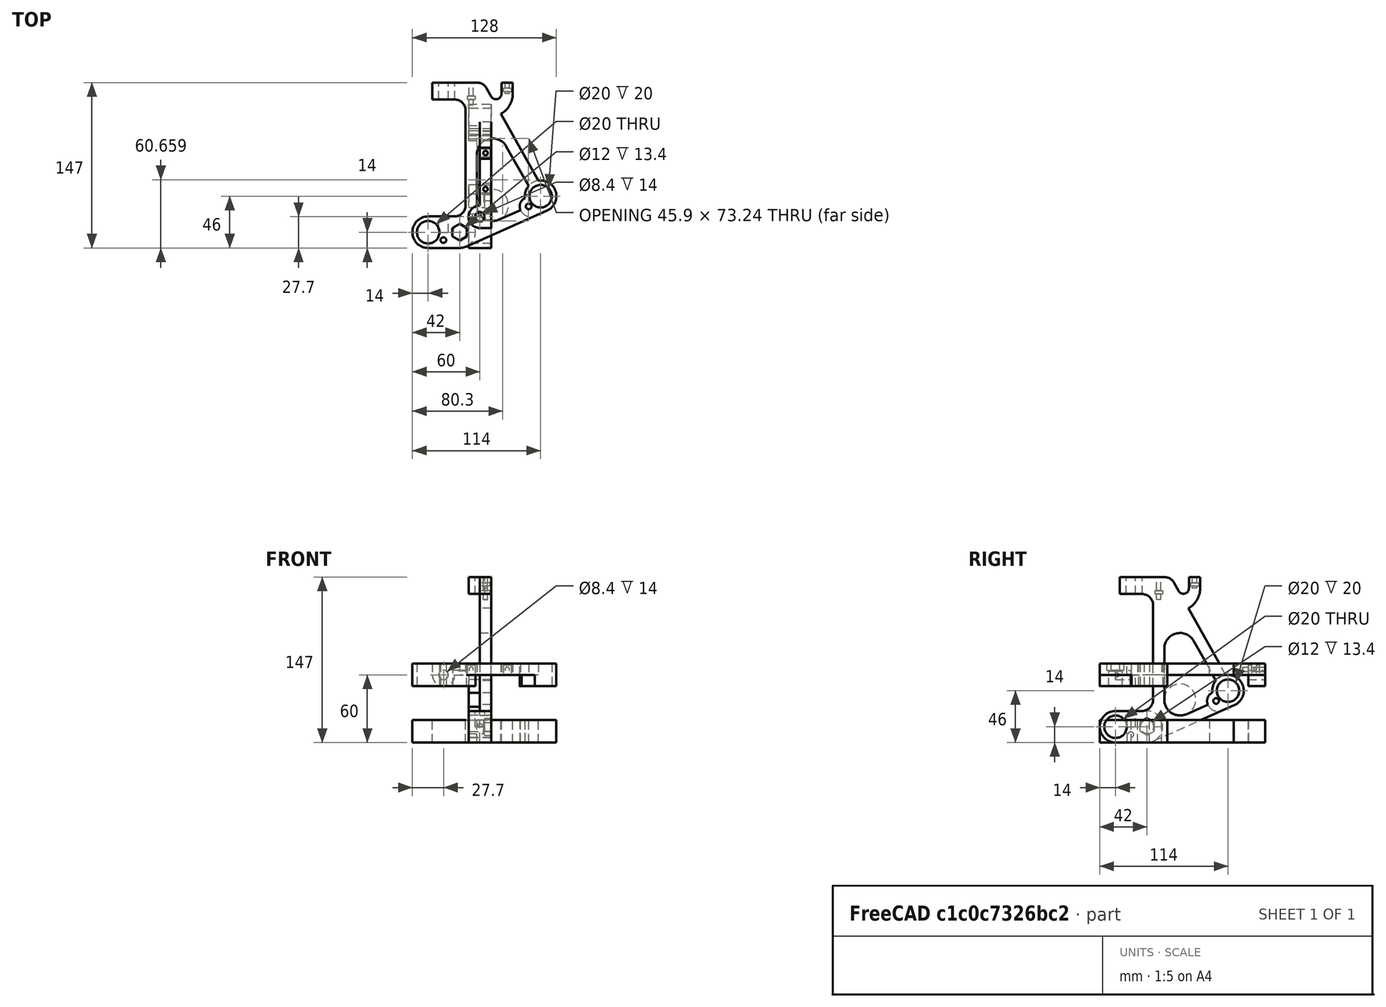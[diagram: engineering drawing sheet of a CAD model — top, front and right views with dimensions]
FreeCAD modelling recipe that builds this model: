
FCSTD DOCUMENT  (FreeCAD 0.15R4527 (Git))
Label: x_carriage_right
License: All rights reserved
LicenseURL: http://en.wikipedia.org/wiki/All_rights_reserved
objects: Part::Cylinder×10, Part::MultiFuse×8, Part::Cut×5, Part::Feature×3, Sketcher::SketchObject×2, Part::Box×2, Part::Extrusion×1, PartDesign::Pocket×1, Mesh::Feature×1, Part::Mirroring×1, Part::Prism×1
note: 35 computed .brp shape members not serialized (recipe doc carries the construction recipe); baked Part::Feature solids carry a one-line shape summary decoded from their .brp

FEATURE [Part::Feature] Xcariageleft001001  label="Xcariageleft002"
  shape: bbox 128 x 147 x 20 mm, 1927 faces, 0 solids (baked)
FEATURE [Sketcher::SketchObject] Sketch
  ExternalGeometry = -> [Xcariageleft001001]
  Placement = pos=(0,0,3.8147e-06) rot=(1,0,0;3.14159rad)
  Support = -> Xcariageleft001001 [Face866]
  sketch-geometry (27):
    g0: LineSegment StartX=14 StartY=-3e-12 StartZ=0 EndX=42 EndY=1e-12 EndZ=0
    g1: LineSegment StartX=47.6883 StartY=-1.20767 StartZ=0 EndX=119.688 EndY=-33.2233 EndZ=0
    g2: LineSegment StartX=111.977 StartY=-59.8687 StartZ=0 EndX=78.7678 EndY=-119.207 EndZ=0
    g3: LineSegment StartX=83.5669 StartY=-90.1556 StartZ=0 EndX=103.25 EndY=-54.9849 EndZ=0
    g4: LineSegment StartX=96.0562 StartY=-33.6591 StartZ=0 EndX=77.0383 EndY=-25.2025 EndZ=0
    g5: LineSegment StartX=57.35 StartY=-37.9949 StartZ=0 EndX=57.35 EndY=-83.3184 EndZ=0
    g6: LineSegment StartX=14 StartY=-28 StartZ=0 EndX=37.35 EndY=-28 EndZ=0
    g7: LineSegment StartX=47.35 StartY=-38 StartZ=0 EndX=47.35 EndY=-122 EndZ=0
    g8: LineSegment StartX=37.35 StartY=-132 StartZ=0 EndX=17.7 EndY=-132 EndZ=0
    g9: ArcOfCircle CenterX=114 CenterY=-46.0156 CenterZ=0 NormalX=0 NormalY=0 NormalZ=1 Radius=14 StartAngle=4.56737 EndAngle=7.43558
    g10: ArcOfCircle CenterX=103.366 CenterY=-36.9095 CenterZ=0 NormalX=0 NormalY=0 NormalZ=1 Radius=8.00001 StartAngle=2.72319 EndAngle=4.29398
    g11: ArcOfCircle CenterX=114 CenterY=-46.0156 CenterZ=0 NormalX=0 NormalY=0 NormalZ=1 Radius=14 StartAngle=3.01294 EndAngle=3.83695
    g12: ArcOfCircle CenterX=71.35 CenterY=-83.3184 CenterZ=0 NormalX=0 NormalY=0 NormalZ=1 Radius=14 StartAngle=3.14159 EndAngle=5.77296
    g13: ArcOfCircle CenterX=68.8096 CenterY=-137 CenterZ=0 NormalX=0 NormalY=0 NormalZ=1 Radius=20.3904 StartAngle=2.53065e-07 EndAngle=1.06057
    g14: ArcOfCircle CenterX=74.3581 CenterY=-137 CenterZ=0 NormalX=0 NormalY=0 NormalZ=1 Radius=4.84187 StartAngle=1.80253e-06 EndAngle=2.63136
    g15: ArcOfCircle CenterX=57.35 CenterY=-137 CenterZ=0 NormalX=0 NormalY=0 NormalZ=1 Radius=10 StartAngle=4.71239 EndAngle=5.77295
    g16: ArcOfCircle CenterX=37.35 CenterY=-122 CenterZ=0 NormalX=0 NormalY=0 NormalZ=1 Radius=10 StartAngle=4.71239 EndAngle=6.28318
    g17: ArcOfCircle CenterX=71.35 CenterY=-37.9949 CenterZ=0 NormalX=0 NormalY=0 NormalZ=1 Radius=14 StartAngle=1.15239 EndAngle=3.14159
    g18: ArcOfCircle CenterX=37.35 CenterY=-38 CenterZ=0 NormalX=0 NormalY=0 NormalZ=1 Radius=10 StartAngle=6.16e-10 EndAngle=1.5708
    g19: ArcOfCircle CenterX=42 CenterY=-13.9999 CenterZ=0 NormalX=0 NormalY=0 NormalZ=1 Radius=13.9999 StartAngle=1.15239 EndAngle=1.5708
    g20: ArcOfCircle CenterX=14 CenterY=-14 CenterZ=0 NormalX=0 NormalY=0 NormalZ=1 Radius=14 StartAngle=1.5708 EndAngle=4.71239
    g21: LineSegment StartX=17.7 StartY=-132 StartZ=0 EndX=17.7 EndY=-147 EndZ=0
    g22: LineSegment StartX=17.7 StartY=-147 StartZ=0 EndX=57.35 EndY=-147 EndZ=0
    g23: LineSegment StartX=70.133 StartY=-134.635 StartZ=0 EndX=66.0763 EndY=-141.884 EndZ=0
    g24: LineSegment StartX=79.2 StartY=-137 StartZ=0 EndX=79.2 EndY=-147 EndZ=0
    g25: LineSegment StartX=89.2 StartY=-137 StartZ=0 EndX=89.2 EndY=-147 EndZ=0
    g26: LineSegment StartX=79.2 StartY=-147 StartZ=0 EndX=89.2 EndY=-147 EndZ=0
  constraints (66):
    c: Coincident(g0,g-4)
    c: Coincident(g0,g-4)
    c: Coincident(g1,g-3)
    c: Coincident(g1,g-3)
    c: Coincident(g2,g-9)
    c: Coincident(g2,g-9)
    c: Coincident(g3,g-8)
    c: Coincident(g3,g-8)
    c: Coincident(g4,g-17)
    c: Coincident(g4,g-17)
    c: Coincident(g5,g-7)
    c: Coincident(g5,g-7)
    c: Coincident(g6,g-5)
    c: Coincident(g6,g-5)
    c: Coincident(g7,g-6)
    c: Coincident(g7,g-6)
    c: Coincident(g8,g-16)
    c: Coincident(g8,g-16)
    c: Coincident(g9,g2)
    c: Coincident(g9,g1)
    c: PointOnObject(g-22,g9)
    c: Coincident(g10,g-20)
    c: Coincident(g10,g4)
    c: PointOnObject(g-19,g10)
    c: Coincident(g11,g10)
    c: Coincident(g11,g3)
    c: PointOnObject(g-21,g11)
    c: Coincident(g12,g5)
    c: Coincident(g12,g3)
    c: PointOnObject(g-27,g12)
    c: Coincident(g13,g2)
    c: Coincident(g13,g-10)
    c: PointOnObject(g-23,g13)
    c: Coincident(g14,g-13)
    c: Coincident(g14,g-12)
    c: PointOnObject(g-24,g14)
    c: Coincident(g15,g-13)
    c: Coincident(g15,g-14)
    c: PointOnObject(g-25,g15)
    c: Coincident(g16,g8)
    c: Coincident(g16,g7)
    c: PointOnObject(g-26,g16)
    c: Coincident(g17,g5)
    c: Coincident(g17,g4)
    c: PointOnObject(g-18,g17)
    c: Coincident(g18,g7)
    c: Coincident(g18,g6)
    c: PointOnObject(g-28,g18)
    c: Coincident(g19,g1)
    c: Coincident(g19,g0)
    c: PointOnObject(g-30,g19)
    c: Coincident(g20,g6)
    c: Coincident(g20,g0)
    c: PointOnObject(g-29,g20)
    c: Coincident(g21,g8)
    c: Coincident(g21,g-15)
    c: Coincident(g22,g21)
    c: Coincident(g22,g15)
    c: Coincident(g23,g14)
    c: Coincident(g23,g15)
    c: Coincident(g24,g14)
    c: Coincident(g24,g-12)
    c: Coincident(g25,g13)
    c: Coincident(g25,g-11)
    c: Coincident(g26,g24)
    c: Coincident(g26,g25)
FEATURE [Part::Cylinder] Cylinder  label="Cilindro"
  Angle = 360
  Height = 15
  Placement = pos=(27.7,132,10) rot=(-1,0,0;1.5708rad)
  Radius = 10
FEATURE [Part::Cylinder] Cylinder001  label="rod_hole"
  Angle = 360
  Height = 15
  Placement = pos=(27.7,132,10) rot=(-1,0,0;1.5708rad)
  Radius = 4.2
FEATURE [Part::Cylinder] Cylinder002  label="Cilindro001"
  Angle = 360
  Height = 22
  Placement = pos=(14,14,-1) rot=(0,0,1;0rad)
  Radius = 10
FEATURE [Part::Cylinder] Cylinder003  label="Cilindro002"
  Angle = 360
  Height = 22
  Placement = pos=(114,46,-1) rot=(0,0,1;0rad)
  Radius = 10
FEATURE [Part::Cylinder] Cylinder004  label="Cilindro003"
  Angle = 360
  Height = 22
  Placement = pos=(42,14,41.4) rot=(0,0,1;0rad)
  Radius = 6
FEATURE [Part::MultiFuse] Fusion003  label="bearing_holes"
  Shapes = -> [Cylinder002,Cylinder003]
FEATURE [Part::Extrusion] Extrude
  Base = -> Sketch
  Dir = (0,0,20)
  Solid = true
FEATURE [Sketcher::SketchObject] Sketch001
  ExternalGeometry = -> [Extrude]
  Placement = pos=(0,0,20) rot=(0,0,1;0rad)
  Support = -> Extrude [Face29]
  sketch-geometry (31):
    g0: LineSegment StartX=37.35 StartY=132 StartZ=0 EndX=17.7 EndY=132 EndZ=0
    g1: LineSegment StartX=17.7 StartY=132 StartZ=0 EndX=17.7 EndY=147 EndZ=0
    g2: LineSegment StartX=17.7 StartY=147 StartZ=0 EndX=57.35 EndY=147 EndZ=0
    g3: LineSegment StartX=79.2 StartY=137 StartZ=0 EndX=79.2 EndY=147 EndZ=0
    g4: LineSegment StartX=89.2 StartY=147 StartZ=0 EndX=89.2 EndY=137 EndZ=0
    g5: ArcOfCircle CenterX=57.35 CenterY=137 CenterZ=0 NormalX=0 NormalY=0 NormalZ=1 Radius=10 StartAngle=0.510231 EndAngle=1.5708
    g6: ArcOfCircle CenterX=68.8096 CenterY=137 CenterZ=0 NormalX=0 NormalY=0 NormalZ=1 Radius=20.3904 StartAngle=5.22262 EndAngle=6.28319
    g7: ArcOfCircle CenterX=74.3581 CenterY=137 CenterZ=0 NormalX=0 NormalY=0 NormalZ=1 Radius=4.84187 StartAngle=3.65182 EndAngle=6.28318
    g8: LineSegment StartX=66.0763 StartY=141.884 StartZ=0 EndX=70.133 EndY=134.635 EndZ=0
    g9: ArcOfCircle CenterX=37.35 CenterY=122 CenterZ=0 NormalX=0 NormalY=0 NormalZ=1 Radius=10 StartAngle=1.08019e-06 EndAngle=1.5708
    g10: LineSegment StartX=79.2 StartY=147 StartZ=0 EndX=89.2 EndY=147 EndZ=0
    g11: LineSegment StartX=47.35 StartY=122 StartZ=0 EndX=47.35 EndY=38 EndZ=0
    g12: LineSegment StartX=57.35 StartY=83.3184 StartZ=0 EndX=57.35 EndY=37.9949 EndZ=0
    g13: ArcOfCircle CenterX=71.35 CenterY=83.3184 CenterZ=0 NormalX=0 NormalY=0 NormalZ=1 Radius=14 StartAngle=0.510228 EndAngle=3.14159
    g14: LineSegment StartX=83.5669 StartY=90.1556 StartZ=0 EndX=103.25 EndY=54.9849 EndZ=0
    g15: LineSegment StartX=77.0383 StartY=25.2025 StartZ=0 EndX=96.0562 EndY=33.6591 EndZ=0
    g16: LineSegment [constr] StartX=57.35 StartY=37.9949 StartZ=0 EndX=71.35 EndY=37.9949 EndZ=0
    g17: LineSegment [constr] StartX=71.35 StartY=37.9949 StartZ=0 EndX=77.0383 EndY=25.2025 EndZ=0
    g18: ArcOfCircle CenterX=71.35 CenterY=37.9949 CenterZ=0 NormalX=0 NormalY=0 NormalZ=1 Radius=14 StartAngle=3.14159 EndAngle=5.13079
    g19: LineSegment [constr] StartX=111.977 StartY=59.8687 StartZ=0 EndX=114 EndY=46.0156 EndZ=0
    g20: ArcOfCircle CenterX=114 CenterY=46.0156 CenterZ=0 NormalX=0 NormalY=0 NormalZ=1 Radius=14 StartAngle=1.71582 EndAngle=2.44623
    g21: LineSegment [constr] StartX=103.366 StartY=36.9095 StartZ=0 EndX=96.0562 EndY=33.6591 EndZ=0
    g22: LineSegment StartX=111.977 StartY=59.8687 StartZ=0 EndX=78.7678 EndY=119.207 EndZ=0
    g23: LineSegment [constr] StartX=119.688 StartY=33.2233 StartZ=0 EndX=108.723 EndY=28.3476 EndZ=0
    g24: ArcOfCircle CenterX=41.9997 CenterY=13.9999 CenterZ=0 NormalX=0 NormalY=0 NormalZ=1 Radius=14.0001 StartAngle=5.13081 EndAngle=7.85396
    g25: LineSegment StartX=37.35 StartY=28 StartZ=0 EndX=42 EndY=28 EndZ=0
    g26: LineSegment [constr] StartX=37.35 StartY=28 StartZ=0 EndX=41.9997 EndY=13.9999 EndZ=0
    g27: ArcOfCircle CenterX=37.35 CenterY=38 CenterZ=0 NormalX=0 NormalY=0 NormalZ=1 Radius=10 StartAngle=4.71239 EndAngle=6.28319
    g28: LineSegment StartX=47.6883 StartY=1.20767 StartZ=0 EndX=108.723 EndY=28.3476 EndZ=0
    g29: ArcOfCircle CenterX=103.366 CenterY=36.9095 CenterZ=0 NormalX=0 NormalY=0 NormalZ=1 Radius=8 StartAngle=3.56 EndAngle=3.8283
    g30: ArcOfCircle CenterX=105.144 CenterY=37.344 CenterZ=0 NormalX=0 NormalY=0 NormalZ=1 Radius=9.68242 StartAngle=3.74652 EndAngle=5.09109
  constraints (78):
    c: Coincident(g0,g-14)
    c: Coincident(g0,g-5)
    c: Coincident(g1,g0)
    c: Coincident(g1,g-6)
    c: Coincident(g2,g1)
    c: Coincident(g2,g-8)
    c: Coincident(g3,g-10)
    c: Coincident(g3,g-11)
    c: Coincident(g4,g-12)
    c: Coincident(g4,g-13)
    c: Coincident(g5,g-8)
    c: Coincident(g5,g2)
    c: Coincident(g5,g-8)
    c: Coincident(g6,g-13)
    c: Coincident(g6,g4)
    c: Coincident(g6,g-15)
    c: Coincident(g7,g-9)
    c: Coincident(g7,g-9)
    c: Coincident(g7,g3)
    c: Coincident(g8,g5)
    c: Coincident(g8,g7)
    c: Coincident(g9,g-14)
    c: Coincident(g9,g0)
    c: Coincident(g9,g-14)
    c: Coincident(g10,g3)
    c: Coincident(g10,g4)
    c: Coincident(g11,g9)
    c: Coincident(g11,g-19)
    c: Coincident(g12,g-18)
    c: Coincident(g13,g-17)
    c: Coincident(g13,g12)
    c: Coincident(g13,g-17)
    c: Coincident(g14,g13)
    c: Coincident(g15,g-21)
    c: Coincident(g16,g12)
    c: Horizontal(g16)
    c: Coincident(g17,g16)
    c: Coincident(g17,g15)
    c: DistanceX(g16) = 14
    c: Equal(g16,g17)
    c: Vertical(g12)
    c: Coincident(g18,g16)
    c: Coincident(g18,g12)
    c: Coincident(g18,g15)
    c: Distance(g19) = 14
    c: Coincident(g20,g19)
    c: Coincident(g20,g19)
    c: Coincident(g19,g-15)
    c: Coincident(g21,g15)
    c: Parallel(g21,g-21)
    c: Distance(g21) = 8
    c: Coincident(g15,g-21)
    c: Coincident(g14,g-16)
    c: Coincident(g22,g19)
    c: Coincident(g22,g6)
    c: Coincident(g23,g-20)
    c: Distance(g23) = 12
    c: PointOnObject(g23,g-20)
    c: Coincident(g25,g-19)
    c: Coincident(g25,g24)
    c: Horizontal(g25)
    c: DistanceX(g25) = 4.65003
    c: Coincident(g26,g25)
    c: Coincident(g26,g24)
    c: Distance(g26) = 14.752
    c: Coincident(g24,g-20)
    c: Coincident(g27,g-19)
    c: Coincident(g27,g25)
    c: Coincident(g27,g11)
    c: Coincident(g28,g24)
    c: Coincident(g28,g23)
    c: Coincident(g29,g21)
    c: Coincident(g29,g15)
    c: Coincident(g30,g23)
    c: Coincident(g29,g30)
    c: Angle(g29) = 0.268297
    c: Coincident(g20,g14)
    c: Angle(g30) = 1.34458
FEATURE [PartDesign::Pocket] Pocket
  Length = 10
  Sketch = -> Sketch001
  Type = 0
FEATURE [Part::MultiFuse] Fusion
  Shapes = -> [Pocket,Cylinder]
FEATURE [Part::Cylinder] Cylinder007  label="Cilindro005"
  Angle = 360
  Height = 22
  Placement = pos=(27.6,7,-1) rot=(0,0,1;0rad)
  Radius = 2.5
FEATURE [Part::Cylinder] Cylinder008  label="Cilindro006"
  Angle = 360
  Height = 22
  Placement = pos=(103.4,36.9,-1) rot=(0,0,1;0rad)
  Radius = 2.5
FEATURE [Part::Cylinder] Cylinder009  label="rod_hole001"
  Angle = 360
  Height = 15
  Placement = pos=(27.7,14,10) rot=(-1,0,0;1.5708rad)
  Radius = 4.2
FEATURE [Part::MultiFuse] Fusion006  label="rod_holes"
  Shapes = -> [Cylinder009,Cylinder001]
FEATURE [Part::MultiFuse] Fusion007  label="joined_holes"
  Shapes = -> [Cylinder008,Cylinder007]
FEATURE [Mesh::Feature] Xcariageright
  Placement = pos=(128,0,0) rot=(0,1,0;3.14159rad)
FEATURE [Part::Feature] Xcariageright001001  label="Xcariageright002"
  Placement = pos=(0,0,70) rot=(0,0,1;0rad)
  shape: bbox 128 x 147 x 20 mm, 969 faces, 0 solids (baked)
FEATURE [Part::Box] Box001  label="Cubo001"
  Height = 10
  Length = 7
  Placement = pos=(80.8,139,1) rot=(0,0,1;0rad)
  Width = 3
FEATURE [Part::Box] Box  label="Cubo"
  Height = 10
  Length = 7
  Placement = pos=(48.8,132,1) rot=(0,0,1;0rad)
  Width = 3
FEATURE [Part::Cylinder] Cylinder011  label="Cilindro008"
  Angle = 360
  Height = 11
  Placement = pos=(84.35,137,5) rot=(-1,0,0;1.5708rad)
  Radius = 2
FEATURE [Part::Cylinder] Cylinder010  label="Cilindro007"
  Angle = 360
  Height = 21
  Placement = pos=(52.35,127,5) rot=(-1,0,0;1.5708rad)
  Radius = 2
FEATURE [Part::MultiFuse] Fusion009  label="nut_holes"
  Shapes = -> [Box,Box001]
FEATURE [Part::MultiFuse] Fusion008  label="screw_holes"
  Shapes = -> [Cylinder010,Cylinder011]
FEATURE [Part::MultiFuse] Fusion010  label="screws_top"
  Shapes = -> [Fusion008,Fusion009]
FEATURE [Part::Cut] Cut
  Base = -> Fusion
  Tool = -> Fusion003
FEATURE [Part::Cut] Cut001
  Base = -> Cut
  Tool = -> Fusion006
FEATURE [Part::Cut] Cut002
  Base = -> Cut001
  Tool = -> Fusion007
FEATURE [Part::Cut] Cut003
  Base = -> Cut002
  Tool = -> Fusion010
FEATURE [Part::Mirroring] Part__Mirroring  label="Cut003 (Mirror #1)"
  Base = (0,0,0)
  Normal = (0,0,1)
  Placement = pos=(0,0,70) rot=(0,0,1;0rad)
  Source = -> Cut003
FEATURE [Part::Prism] Prism  label="Prisma"
  Circumradius = 7.55
  Height = 7
  Placement = pos=(42,14,64) rot=(0,0,1;0.523599rad)
  Polygon = 6
FEATURE [Part::MultiFuse] Fusion011  label="threaded_rod_hole"
  Shapes = -> [Prism,Cylinder004]
FEATURE [Part::Cut] Cut004  label="x_carriage_right"
  Base = -> Part__Mirroring
  Tool = -> Fusion011
FEATURE [Part::Feature] Cut004001  label="x_carriage_right001"
  Placement = pos=(0,0,0) rot=(0.57735,0.57735,0.57735;2.0944rad)
  shape: bbox 20 x 128 x 147 mm, 71 faces (baked)
